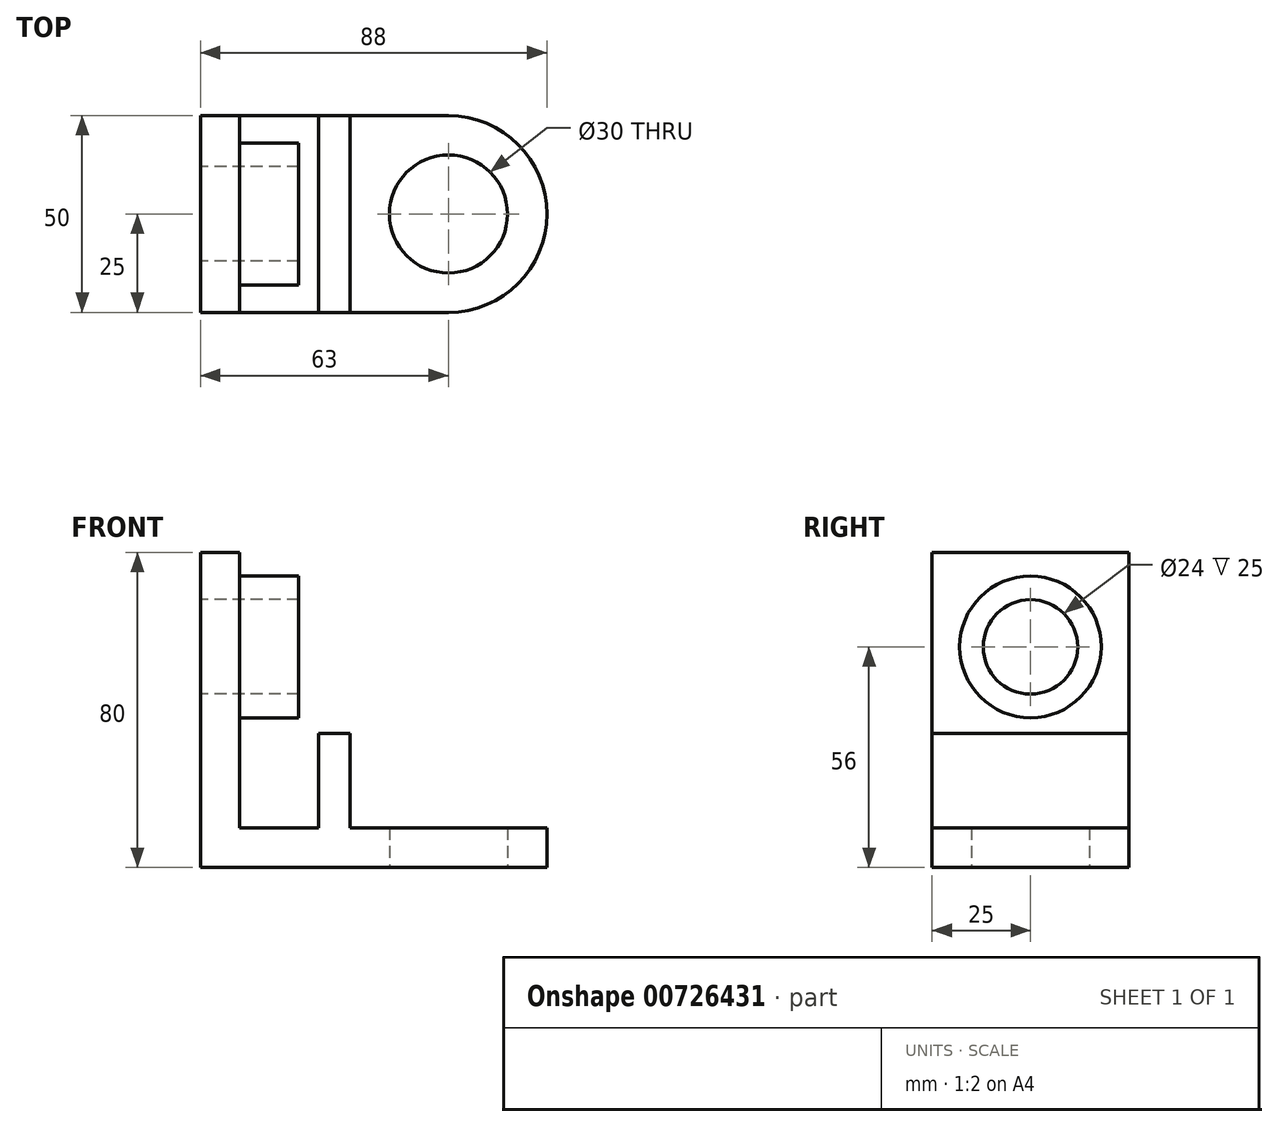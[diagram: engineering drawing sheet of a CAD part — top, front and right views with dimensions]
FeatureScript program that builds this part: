
annotation { "Feature Type Name" : "Feature", "Feature Type Description" : "" }
export const myFeature = defineFeature(function(context is Context, id is Id, definition is map)
    precondition{}
    {
        {
            var Q0;
            Q0=qCreatedBy(makeId("Top.planeOp"),FACE);
            var sketch = newSketch(context, id + "F0", { "sketchPlane" : qUnion([Q0])});
            skLineSegment(sketch, "E0.bottom", {"start": v(0, 0) * mm, "end": v(63, 0) * mm});
            skLineSegment(sketch, "E0.top", {"start": v(0, 50) * mm, "end": v(63, 50) * mm});
            skLineSegment(sketch, "E0.left", {"start": v(0, 0) * mm, "end": v(0, 50) * mm});
            skLineSegment(sketch, "E0.right", {"start": v(63, 10) * mm, "end": v(63, 40) * mm});
            skArc(sketch, "E1", {"start": v(63, 0) * mm, "mid": v(88, 25) * mm, "end": v(63, 50) * mm});
            skCircle(sketch, "E2", {"center": v(63, 25) * mm, "radius": 15 * mm});
            skSolve(sketch);
        }
        {
            var Q0;
            Q0 = qSketchRegion(id + "F0", true);
            extrude(context, id + "F1", {"entities" : qUnion([Q0]), "depth" : 10 * mm, "offsetDistance" : 25 * mm});
        }
        {
            var Q0;
            Q0=makeQuery(id+"F1.opExtrude","CAP_FACE",FACE,{"disambiguationData":[OSD([sQuery(id+"F0.wireOp",EDGE,"E0.bottom"),sQuery(id+"F0.wireOp",EDGE,"E0.top"),sQuery(id+"F0.wireOp",EDGE,"E0.left"),sQuery(id+"F0.wireOp",EDGE,"E1"),sQuery(id+"F0.wireOp",EDGE,"E2")])],"isStart":false});
            var sketch = newSketch(context, id + "F2", { "sketchPlane" : qUnion([Q0])});
            skLineSegment(sketch, "E3", {"start": v(0, 0) * mm, "end": v(30, 0) * mm});
            skLineSegment(sketch, "E4.bottom", {"start": v(30, 0) * mm, "end": v(38, 0) * mm});
            skLineSegment(sketch, "E4.top", {"start": v(30, 50) * mm, "end": v(38, 50) * mm});
            skLineSegment(sketch, "E4.left", {"start": v(30, 0) * mm, "end": v(30, 50) * mm});
            skLineSegment(sketch, "E4.right", {"start": v(38, 0) * mm, "end": v(38, 50) * mm});
            skSolve(sketch);
        }
        {
            var Q0;
            Q0 = qSketchRegion(id + "F2", true);
            extrude(context, id + "F3", {"entities" : qUnion([Q0]), "operationType" : NewBodyOperationType.ADD, "depth" : 24 * mm, "offsetDistance" : 25 * mm});
        }
        {
            var Q0;
            {var subQ0=sQuery(id+"F0.wireOp",EDGE,"E0.left");var subQ1=sQuery(id+"F0.wireOp",EDGE,"E0.top");var subQ2=sQuery(id+"F0.wireOp",EDGE,"E0.bottom");Q0=makeQuery(id+"F3.boolean.opBoolean","SPLIT",FACE,{"disambiguationData":[TD([makeQuery(id+"F1.opExtrude","SWEPT_FACE",FACE,{"disambiguationData":[OSD([subQ0])]})])],"derivedFrom":makeQuery(id+"F1.opExtrude","CAP_FACE",FACE,{"disambiguationData":[OSD([subQ2,subQ1,subQ0,sQuery(id+"F0.wireOp",EDGE,"E1"),sQuery(id+"F0.wireOp",EDGE,"E2")])],"isStart":false})});}
            var sketch = newSketch(context, id + "F4", { "sketchPlane" : qUnion([Q0])});
            skLineSegment(sketch, "E5.bottom", {"start": v(0, 0) * mm, "end": v(10, 0) * mm});
            skLineSegment(sketch, "E5.top", {"start": v(0, 50) * mm, "end": v(10, 50) * mm});
            skLineSegment(sketch, "E5.left", {"start": v(0, 0) * mm, "end": v(0, 50) * mm});
            skLineSegment(sketch, "E5.right", {"start": v(10, 0) * mm, "end": v(10, 50) * mm});
            skSolve(sketch);
        }
        {
            var Q0;
            Q0 = qSketchRegion(id + "F4", true);
            extrude(context, id + "F5", {"entities" : qUnion([Q0]), "operationType" : NewBodyOperationType.ADD, "depth" : 70 * mm, "offsetDistance" : 25 * mm});
        }
        {
            var Q0;
            Q0=makeQuery(id+"F5.opExtrude","SWEPT_FACE",FACE,{"disambiguationData":[OSD([sQuery(id+"F4.wireOp",EDGE,"E5.right")])]});
            var sketch = newSketch(context, id + "F6", { "sketchPlane" : qUnion([Q0])});
            skLineSegment(sketch, "E6", {"start": v(0, 0) * mm, "end": v(0, 56) * mm});
            skCircle(sketch, "E7", {"center": v(25, 56) * mm, "radius": 18 * mm});
            skCircle(sketch, "E8", {"center": v(25, 56) * mm, "radius": 12 * mm});
            skSolve(sketch);
        }
        {
            var Q0;
            Q0 = qSketchRegion(id + "F6", true);
            extrude(context, id + "F7", {"entities" : qUnion([Q0]), "operationType" : NewBodyOperationType.ADD, "depth" : 15 * mm, "offsetDistance" : 25 * mm});
        }
        {
            var Q0;
            Q0=makeQuery(id+"F7.boolean.opBoolean","SPLIT",FACE,{"disambiguationData":[TD([makeQuery(id+"F7.opExtrude","SWEPT_FACE",FACE,{"disambiguationData":[OSD([sQuery(id+"F6.wireOp",EDGE,"E8")])]})])],"derivedFrom":makeQuery(id+"F5.opExtrude","SWEPT_FACE",FACE,{"disambiguationData":[OSD([sQuery(id+"F4.wireOp",EDGE,"E5.right")])]})});
            var sketch = newSketch(context, id + "F8", { "sketchPlane" : qUnion([Q0])});
            skCircle(sketch, "E9", {"center": v(25, 56) * mm, "radius": 12 * mm});
            skSolve(sketch);
        }
        {
            var Q0;
            Q0 = qSketchRegion(id + "F8", true);
            extrude(context, id + "F9", {"entities" : qUnion([Q0]), "operationType" : NewBodyOperationType.REMOVE, "endBound" : BoundingType.UP_TO_NEXT, "oppositeDirection" : true, "depth" : 25 * mm, "offsetDistance" : 25 * mm});
        }
    });
